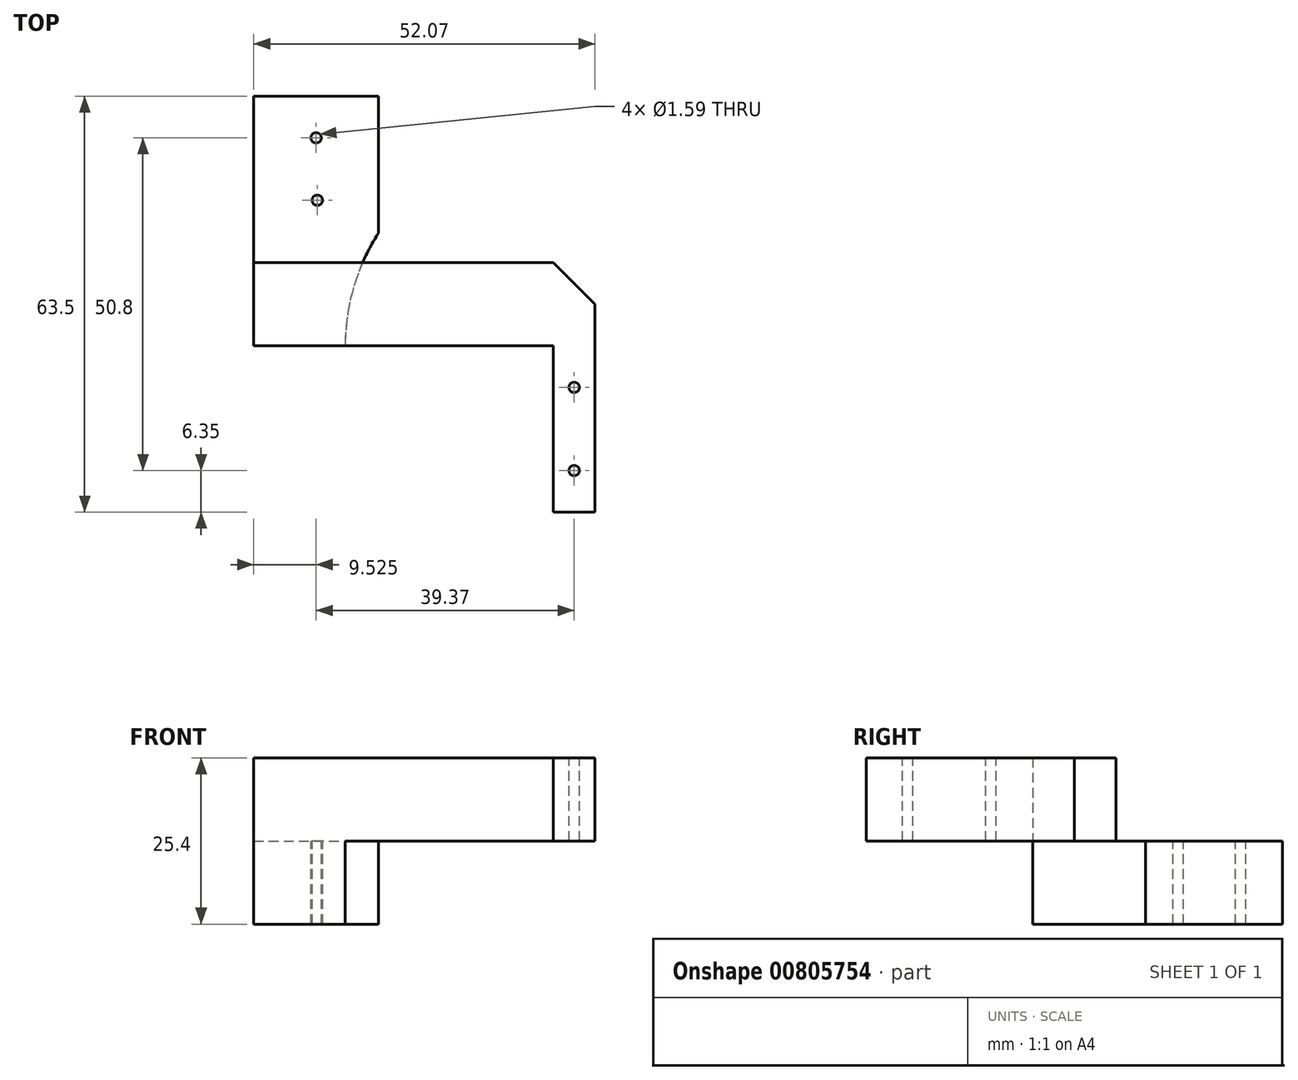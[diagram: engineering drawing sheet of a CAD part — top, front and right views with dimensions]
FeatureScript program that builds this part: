
annotation { "Feature Type Name" : "Feature", "Feature Type Description" : "" }
export const myFeature = defineFeature(function(context is Context, id is Id, definition is map)
    precondition{}
    {
        {
            var Q0;
            Q0=qCreatedBy(makeId("Top.planeOp"),FACE);
            var sketch = newSketch(context, id + "F0", { "sketchPlane" : qUnion([Q0])});
            skLineSegment(sketch, "E0.bottom", {"start": v(0, 12.7) * mm, "end": v(52.07, 12.7) * mm});
            skLineSegment(sketch, "E0.top", {"start": v(0, 0) * mm, "end": v(45.72, 0) * mm});
            skLineSegment(sketch, "E0.left", {"start": v(0, 12.7) * mm, "end": v(0, 0) * mm});
            skLineSegment(sketch, "E0.right", {"start": v(52.07, 12.7) * mm, "end": v(52.07, 0) * mm});
            skLineSegment(sketch, "E1.bottom", {"start": v(52.07, 12.7) * mm, "end": v(45.72, 12.7) * mm});
            skLineSegment(sketch, "E1.top", {"start": v(52.07, -25.4) * mm, "end": v(45.72, -25.4) * mm});
            skLineSegment(sketch, "E1.left", {"start": v(52.07, 12.7) * mm, "end": v(52.07, -25.4) * mm});
            skLineSegment(sketch, "E1.right", {"start": v(45.72, 0) * mm, "end": v(45.72, -25.4) * mm});
            skLineSegment(sketch, "E2.bottom", {"start": v(0, 12.7) * mm, "end": v(19.05, 12.7) * mm});
            skLineSegment(sketch, "E2.top", {"start": v(0, 38.1) * mm, "end": v(19.05, 38.1) * mm});
            skLineSegment(sketch, "E2.left", {"start": v(0, 12.7) * mm, "end": v(0, 38.1) * mm});
            skLineSegment(sketch, "E2.right", {"start": v(19.05, 12.7) * mm, "end": v(19.05, 38.1) * mm});
            skLineSegment(sketch, "E3", {"start": v(19.05, 12.7) * mm, "end": v(19.05, 0) * mm});
            skLineSegment(sketch, "E4", {"start": v(45.72, 12.7) * mm, "end": v(19.05, 38.1) * mm});
            skLineSegment(sketch, "E5", {"start": v(45.72, 12.7) * mm, "end": v(45.72, 0) * mm});
            skCircle(sketch, "E6", {"center": v(45.72, 0) * mm, "radius": 31.75 * mm});
            skSolve(sketch);
        }
        {
            var Q0;
            {var subQ0=sQuery(id+"F0.wireOp",EDGE,"E3");Q0=makeQuery(id+"F0.imprint","IMPRINT",FACE,{"disambiguationData":[TD([[makeQuery(id+"F0.imprint","IMPRINT",EDGE,{"derivedFrom":subQ0}),1.0]])]});}
            var Q1;
            {var subQ0=sQuery(id+"F0.wireOp",EDGE,"E0.left");Q1=makeQuery(id+"F0.imprint","IMPRINT",FACE,{"disambiguationData":[TD([[makeQuery(id+"F0.imprint","IMPRINT",EDGE,{"derivedFrom":subQ0}),1.0]])]});}
            var Q2;
            {var subQ0=sQuery(id+"F0.wireOp",EDGE,"E0.right");Q2=makeQuery(id+"F0.imprint","IMPRINT",FACE,{"disambiguationData":[TD([[makeQuery(id+"F0.imprint","IMPRINT",EDGE,{"derivedFrom":subQ0}),-1.0]])]});}
            var Q3;
            {var subQ0=sQuery(id+"F0.wireOp",EDGE,"E3");Q3=makeQuery(id+"F0.imprint","IMPRINT",FACE,{"disambiguationData":[TD([[makeQuery(id+"F0.imprint","IMPRINT",EDGE,{"derivedFrom":subQ0}),-1.0]])]});}
            extrude(context, id + "F1", {"entities" : qUnion([Q0, Q1, Q2, Q3]), "depth" : 12.7 * mm, "offsetDistance" : 25.4 * mm});
        }
        {
            var Q0;
            {var subQ0=sQuery(id+"F0.wireOp",EDGE,"E0.left");Q0=makeQuery(id+"F0.imprint","IMPRINT",FACE,{"disambiguationData":[TD([[makeQuery(id+"F0.imprint","IMPRINT",EDGE,{"derivedFrom":subQ0}),1.0]])]});}
            var Q1;
            {var subQ1=sQuery(id+"F0.wireOp",EDGE,"E2.top");Q1=makeQuery(id+"F0.imprint","IMPRINT",FACE,{"disambiguationData":[TD([[makeQuery(id+"F0.imprint","IMPRINT",EDGE,{"derivedFrom":subQ1}),-1.0]])]});}
            extrude(context, id + "F2", {"entities" : qUnion([Q0, Q1]), "operationType" : NewBodyOperationType.ADD, "oppositeDirection" : true, "depth" : 12.7 * mm, "offsetDistance" : 25.4 * mm});
        }
        {
            var Q0;
            Q0=makeQuery(id+"F1.opExtrude","SWEPT_EDGE",EDGE,{"disambiguationData":[OSD([sQuery(id+"F0.wireOp",EDGE,"E0.bottom"),sQuery(id+"F0.wireOp",EDGE,"E0.right")])]});
            chamfer(context, id + "F3", {"entities" : qUnion([Q0]), "width" : 6.35 * mm, "tangentPropagation" : true});
        }
        {
            var Q0;
            Q0=makeQuery(id+"F1.opExtrude","CAP_FACE",FACE,{"disambiguationData":[OSD([sQuery(id+"F0.wireOp",EDGE,"E0.bottom"),sQuery(id+"F0.wireOp",EDGE,"E0.top"),sQuery(id+"F0.wireOp",EDGE,"E0.left"),sQuery(id+"F0.wireOp",EDGE,"E0.right"),sQuery(id+"F0.wireOp",EDGE,"E1.top"),sQuery(id+"F0.wireOp",EDGE,"E1.left"),sQuery(id+"F0.wireOp",EDGE,"E1.right")])],"isStart":false});
            var sketch = newSketch(context, id + "F4", { "sketchPlane" : qUnion([Q0])});
            skCircle(sketch, "E7", {"center": v(48.9, -19.05) * mm, "radius": 0.8 * mm});
            skPoint(sketch, "E7.centerSnap0", {"position": v(48.9, -25.4) * mm});
            skCircle(sketch, "E8", {"center": v(48.9, -6.35) * mm, "radius": 0.8 * mm});
            skSolve(sketch);
        }
        {
            var Q0;
            Q0=makeQuery(id+"F4.imprint","IMPRINT",FACE,{"disambiguationData":[TD([[makeQuery(id+"F4.imprint","IMPRINT",EDGE,{"derivedFrom":sQuery(id+"F4.wireOp",EDGE,"E8")}),1.0]])]});
            var Q1;
            Q1=makeQuery(id+"F4.imprint","IMPRINT",FACE,{"disambiguationData":[TD([[makeQuery(id+"F4.imprint","IMPRINT",EDGE,{"derivedFrom":sQuery(id+"F4.wireOp",EDGE,"E7")}),1.0]])]});
            extrude(context, id + "F5", {"entities" : qUnion([Q0, Q1]), "operationType" : NewBodyOperationType.REMOVE, "endBound" : BoundingType.THROUGH_ALL, "oppositeDirection" : true, "depth" : 25.4 * mm, "offsetDistance" : 25.4 * mm});
        }
        {
            var Q0;
            Q0=makeQuery(id+"F2.opExtrude","CAP_FACE",FACE,{"disambiguationData":[OSD([sQuery(id+"F0.wireOp",EDGE,"E0.top"),sQuery(id+"F0.wireOp",EDGE,"E0.left"),sQuery(id+"F0.wireOp",EDGE,"E2.top"),sQuery(id+"F0.wireOp",EDGE,"E2.left"),sQuery(id+"F0.wireOp",EDGE,"E2.right"),sQuery(id+"F0.wireOp",EDGE,"E6")])],"isStart":true});
            var sketch = newSketch(context, id + "F6", { "sketchPlane" : qUnion([Q0])});
            skCircle(sketch, "E9", {"center": v(9.52, 31.75) * mm, "radius": 0.8 * mm});
            skCircle(sketch, "E10", {"center": v(9.71, 22.23) * mm, "radius": 0.8 * mm});
            skSolve(sketch);
        }
        {
            var Q0;
            Q0=makeQuery(id+"F6.imprint","IMPRINT",FACE,{"disambiguationData":[TD([[makeQuery(id+"F6.imprint","IMPRINT",EDGE,{"derivedFrom":sQuery(id+"F6.wireOp",EDGE,"E9")}),1.0]])]});
            var Q1;
            Q1=makeQuery(id+"F6.imprint","IMPRINT",FACE,{"disambiguationData":[TD([[makeQuery(id+"F6.imprint","IMPRINT",EDGE,{"derivedFrom":sQuery(id+"F6.wireOp",EDGE,"E10")}),1.0]])]});
            extrude(context, id + "F7", {"entities" : qUnion([Q0, Q1]), "operationType" : NewBodyOperationType.REMOVE, "endBound" : BoundingType.THROUGH_ALL, "oppositeDirection" : true, "depth" : 25.4 * mm, "offsetDistance" : 25.4 * mm});
        }
    });
